# Revit family: 58_E750109
name_source: partatom
category: Equipos especializados
units: mm (PartAtom-declared; Revit-internal decimal feet)

## family parameters
Compartido = No
Corte con vacíos al cargar = No
Cota de conector redondo = Diámetro de uso
Punto de cálculo de habitación = No
Se basa en plano de trabajo = No
Siempre vertical = Sí
Tipo de pieza = Normal

## types (1)
- E750109
    Aislación = Triple Capa
    Alto = 59.8 cm
    Ancho = 59.8 cm
    Aprobaciones = CE/GS/CB/SAA
    Asa Puerta de Horno = Iron, Gray
    Asa Tope = Tapa Asa
    Color Logo = Logo
    Convección = Forzada
    Creado por = Unibim
    Cuerpo Horno = Steel, Galvanized
    Descripción = Horno eléctrico empotrable, marca Vatti, modelo E750109
    Display = White Soft Touch Led
    Elevación por defecto = 0 cm
    Especificación Técnica = Horno eléctrico empotrable, marca Vatti, modelo E750109
    Fabricante = Vatti
    Facilidad de Uso = 8 programas de cocción
    Fondo = 55.5 cm
    Grill = Doble
    Instalación = Empotrado
    Luz Interior = Sí
    Modelo = E750109
    Modo de Control = Control Digital y Perillas de Presión
    Panel Control = Panel Negro
    Panel Control Cubierta = Panel Vidrio
    Paneles = Vidrio - Acero Inox
    Perilla Exterior = Acero Inox
    Perilla Interior = Perilla Negro
    Peso = 32,3 Kg
    Potencia = 2880 W
    Puerta Interior = Interior Negro
    Puerta Negro = Panel Negro
    Puerta Vidiro = Panel Vidrio
    Rieles para bandejas = Multiposición en cuerpo
    Sello puerta = Perimetral 100%
    Tamaño del corte en superficie = 598 x 598
    Tamaño del producto = 598 x 598 x 555
    Temperatura Máxima = 250° C
    Temporizador = Sí
    Termostato con luz indicadora = Sí
    Timer = con Autoapagado
    Tirador de puerta = Acero Inox
    URL = www.vatti.cl
    Vidrio interior desmontable = Easy Clean
    Voltage / Frecuencia = 220 V
    Volumen interior = 75 Litros

## geometry (parser evidence)
native form markers: Sweep x5
no freeform markers — native parametric forms only
